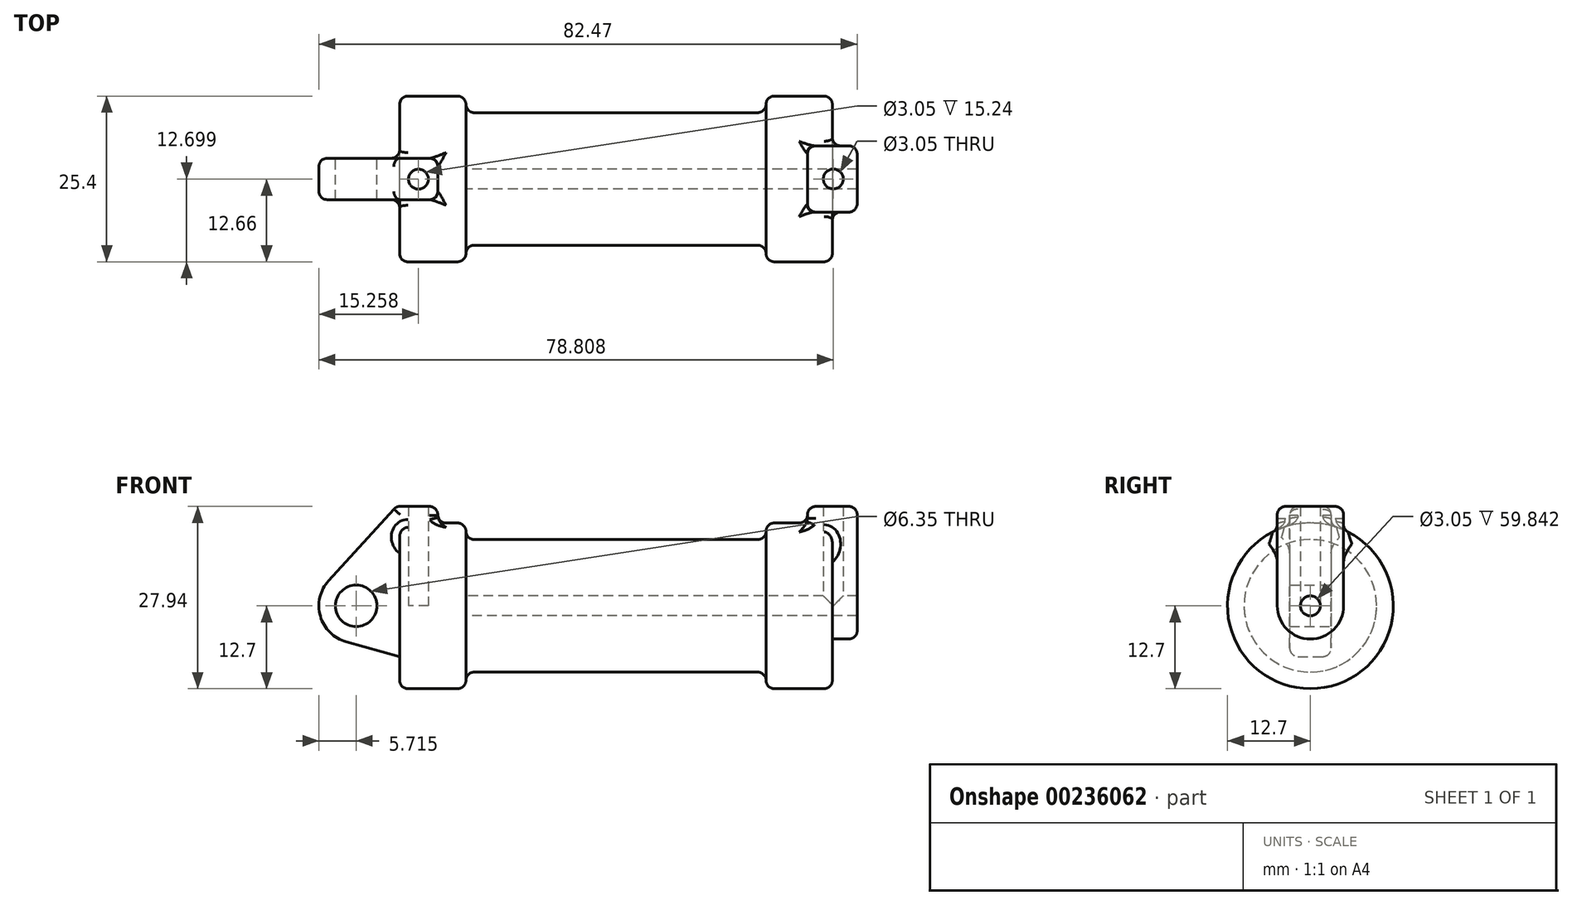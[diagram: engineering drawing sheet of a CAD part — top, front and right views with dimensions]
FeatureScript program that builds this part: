
annotation { "Feature Type Name" : "Feature", "Feature Type Description" : "" }
export const myFeature = defineFeature(function(context is Context, id is Id, definition is map)
    precondition{}
    {
        {
            var Q0;
            Q0=qCreatedBy(makeId("Front.planeOp"),FACE);
            var sketch = newSketch(context, id + "F0", { "sketchPlane" : qUnion([Q0])});
            skLineSegment(sketch, "E0", {"start": v(0, 0) * mm, "end": v(0, 12.7) * mm});
            skLineSegment(sketch, "E1", {"start": v(0, 12.7) * mm, "end": v(10.16, 12.7) * mm});
            skLineSegment(sketch, "E2", {"start": v(10.16, 12.7) * mm, "end": v(10.16, 10.16) * mm});
            skLineSegment(sketch, "E3", {"start": v(10.16, 10.16) * mm, "end": v(56.13, 10.16) * mm});
            skLineSegment(sketch, "E4", {"start": v(56.13, 10.16) * mm, "end": v(56.13, 12.7) * mm});
            skLineSegment(sketch, "E5", {"start": v(56.13, 12.7) * mm, "end": v(66.3, 12.7) * mm});
            skLineSegment(sketch, "E6", {"start": v(66.3, 12.7) * mm, "end": v(66.3, 0) * mm});
            skLineSegment(sketch, "E7", {"start": v(66.3, 0) * mm, "end": v(0, 0) * mm});
            skLineSegment(sketch, "E8", {"start": v(5.84, 15.24) * mm, "end": v(-0.5, 15.24) * mm});
            skLineSegment(sketch, "E9", {"start": v(-0.5, 15.24) * mm, "end": v(-10.88, 3.85) * mm});
            skLineSegment(sketch, "E10", {"start": v(0, 0) * mm, "end": v(-6.65, 0) * mm});
            skCircle(sketch, "E11", {"center": v(-6.65, 0) * mm, "radius": 5.72 * mm});
            skCircle(sketch, "E12", {"center": v(-6.65, 0) * mm, "radius": 3.18 * mm});
            skLineSegment(sketch, "E13", {"start": v(5.84, 15.24) * mm, "end": v(5.84, -9.4) * mm});
            skLineSegment(sketch, "E14", {"start": v(5.84, -9.4) * mm, "end": v(-8.18, -5.5) * mm});
            skSolve(sketch);
        }
        {
            var Q0;
            {var subQ0=sQuery(id+"F0.wireOp",EDGE,"E2");Q0=makeQuery(id+"F0.imprint","IMPRINT",FACE,{"disambiguationData":[TD([[makeQuery(id+"F0.imprint","IMPRINT",EDGE,{"derivedFrom":subQ0}),-1.0]])]});}
            var Q1;
            {var subQ0=sQuery(id+"F0.wireOp",EDGE,"E0");Q1=makeQuery(id+"F0.imprint","IMPRINT",FACE,{"disambiguationData":[TD([[makeQuery(id+"F0.imprint","IMPRINT",EDGE,{"derivedFrom":subQ0}),-1.0]])]});}
            var Q2;
            Q2=sQuery(id+"F0.wireOp",EDGE,"E7");
            revolve(context, id + "F1", {"entities" : qUnion([Q0, Q1]), "axis" : qUnion([Q2]), "revolveType" : RevolveType.FULL});
        }
        {
            var Q0;
            {var subQ0=sQuery(id+"F0.wireOp",EDGE,"E14");Q0=makeQuery(id+"F0.imprint","IMPRINT",FACE,{"disambiguationData":[TD([[makeQuery(id+"F0.imprint","IMPRINT",EDGE,{"derivedFrom":subQ0}),-1.0]])]});}
            var Q1;
            {var subQ4=sQuery(id+"F0.wireOp",EDGE,"E12");Q1=makeQuery(id+"F0.imprint","IMPRINT",FACE,{"disambiguationData":[TD([[makeQuery(id+"F0.imprint","IMPRINT",EDGE,{"derivedFrom":subQ4}),-1.0]])]});}
            var Q2;
            {var subQ3=sQuery(id+"F0.wireOp",EDGE,"E0");Q2=makeQuery(id+"F0.imprint","IMPRINT",FACE,{"disambiguationData":[TD([[makeQuery(id+"F0.imprint","IMPRINT",EDGE,{"derivedFrom":subQ3}),1.0]])]});}
            var Q3;
            {var subQ0=sQuery(id+"F0.wireOp",EDGE,"E0");Q3=makeQuery(id+"F0.imprint","IMPRINT",FACE,{"disambiguationData":[TD([[makeQuery(id+"F0.imprint","IMPRINT",EDGE,{"derivedFrom":subQ0}),-1.0]])]});}
            extrude(context, id + "F2", {"entities" : qUnion([Q0, Q1, Q2, Q3]), "operationType" : NewBodyOperationType.ADD, "endBound" : BoundingType.SYMMETRIC, "depth" : 6.35 * mm});
        }
        {
            var Q0;
            Q0=makeQuery(id+"F1.opRevolve","SWEPT_FACE",FACE,{"disambiguationData":[OSD([sQuery(id+"F0.wireOp",EDGE,"E6")])]});
            var sketch = newSketch(context, id + "F3", { "sketchPlane" : qUnion([Q0])});
            skCircle(sketch, "E15", {"center": v(0, 0) * mm, "radius": 5.08 * mm});
            skCircle(sketch, "E16", {"center": v(0, 0) * mm, "radius": 1.52 * mm});
            skLineSegment(sketch, "E17", {"start": v(5.08, 0) * mm, "end": v(5.08, 15.24) * mm});
            skLineSegment(sketch, "E18", {"start": v(-5.08, 0) * mm, "end": v(-5.08, 15.24) * mm});
            skLineSegment(sketch, "E19", {"start": v(-5.08, 15.24) * mm, "end": v(5.08, 15.24) * mm});
            skSolve(sketch);
        }
        {
            var Q0;
            Q0 = qSketchRegion(id + "F3", true);
            extrude(context, id + "F4", {"entities" : qUnion([Q0]), "operationType" : NewBodyOperationType.ADD, "endBound" : BoundingType.SYMMETRIC, "depth" : 7.62 * mm});
        }
        {
            var Q0;
            Q0=makeQuery(id+"F4.boolean.opBoolean","SPLIT",FACE,{"disambiguationData":[TD([makeQuery(id+"F4.opExtrude","SWEPT_FACE",FACE,{"disambiguationData":[OSD([sQuery(id+"F3.wireOp",EDGE,"E16")])]})])],"derivedFrom":makeQuery(id+"F1.opRevolve","SWEPT_FACE",FACE,{"disambiguationData":[OSD([sQuery(id+"F0.wireOp",EDGE,"E6")])]})});
            extrude(context, id + "F5", {"entities" : qUnion([Q0]), "operationType" : NewBodyOperationType.REMOVE, "oppositeDirection" : true, "depth" : 56.03 * mm});
        }
        {
            var Q0;
            Q0=qCreatedBy(makeId("Top.planeOp"),FACE);
            var sketch = newSketch(context, id + "F6", { "sketchPlane" : qUnion([Q0])});
            skCircle(sketch, "E20", {"center": v(2.89, -0.04) * mm, "radius": 1.52 * mm});
            skSolve(sketch);
        }
        {
            var Q0;
            Q0 = qSketchRegion(id + "F6", true);
            extrude(context, id + "F7", {"entities" : qUnion([Q0]), "operationType" : NewBodyOperationType.REMOVE, "depth" : 17.78 * mm});
        }
        {
            var Q0;
            Q0=qCreatedBy(makeId("Top.planeOp"),FACE);
            var sketch = newSketch(context, id + "F8", { "sketchPlane" : qUnion([Q0])});
            skCircle(sketch, "E21", {"center": v(66.44, 0) * mm, "radius": 1.52 * mm});
            skSolve(sketch);
        }
        {
            var Q0;
            Q0 = qSketchRegion(id + "F8", true);
            extrude(context, id + "F9", {"entities" : qUnion([Q0]), "operationType" : NewBodyOperationType.REMOVE, "depth" : 15.75 * mm});
        }
        {
            var Q0;
            Q0=makeQuery(id+"F1.opRevolve","SWEPT_FACE",FACE,{"disambiguationData":[OSD([sQuery(id+"F0.wireOp",EDGE,"E3")])]});
            var Q1;
            Q1=makeQuery(id+"F1.opRevolve","SWEPT_FACE",FACE,{"disambiguationData":[OSD([sQuery(id+"F0.wireOp",EDGE,"E5")])]});
            var Q2;
            Q2=makeQuery(id+"F1.opRevolve","SWEPT_FACE",FACE,{"disambiguationData":[OSD([sQuery(id+"F0.wireOp",EDGE,"E1")])]});
            fillet(context, id + "F10", {"entities" : qUnion([Q0, Q1, Q2]), "radius" : 1.27 * mm, "tangentPropagation" : true, "allowEdgeOverflow" : false});
        }
        {
            var Q0;
            Q0=makeQuery(id+"F2.opExtrude","CAP_EDGE",EDGE,{"disambiguationData":[OSD([sQuery(id+"F0.wireOp",EDGE,"E9")])],"isStart":false});
            var Q1;
            Q1=makeQuery(id+"F2.opExtrude","CAP_EDGE",EDGE,{"disambiguationData":[OSD([sQuery(id+"F0.wireOp",EDGE,"E8")])],"isStart":false});
            var Q2;
            Q2=makeQuery(id+"F2.opExtrude","CAP_EDGE",EDGE,{"disambiguationData":[OSD([sQuery(id+"F0.wireOp",EDGE,"E13")])],"isStart":false});
            var Q3;
            {var subQ0=makeQuery(id+"F2.opExtrude","CAP_FACE",FACE,{"disambiguationData":[OSD([sQuery(id+"F0.wireOp",EDGE,"E8"),sQuery(id+"F0.wireOp",EDGE,"E9"),sQuery(id+"F0.wireOp",EDGE,"E11"),sQuery(id+"F0.wireOp",EDGE,"E12"),sQuery(id+"F0.wireOp",EDGE,"E13"),sQuery(id+"F0.wireOp",EDGE,"E14")])],"isStart":false});Q3=makeQuery(id+"F10.opFillet","BLEND_EDGE",EDGE,{"blendedFrom":[makeQuery(id+"F2.boolean.opBoolean","INTERSECT",EDGE,{"derivedFrom":[makeQuery(id+"F1.opRevolve","SWEPT_FACE",FACE,{"disambiguationData":[OSD([sQuery(id+"F0.wireOp",EDGE,"E1")])]}),subQ0]}),subQ0],"blendedInto":[subQ0]});}
            var Q4;
            {var subQ0=makeQuery(id+"F2.opExtrude","CAP_FACE",FACE,{"disambiguationData":[OSD([sQuery(id+"F0.wireOp",EDGE,"E8"),sQuery(id+"F0.wireOp",EDGE,"E9"),sQuery(id+"F0.wireOp",EDGE,"E11"),sQuery(id+"F0.wireOp",EDGE,"E12"),sQuery(id+"F0.wireOp",EDGE,"E13"),sQuery(id+"F0.wireOp",EDGE,"E14")])],"isStart":false});Q4=makeQuery(id+"F10.opFillet","BLEND_EDGE",EDGE,{"blendedFrom":[makeQuery(id+"F2.boolean.opBoolean","INTERSECT",VERTEX,{"derivedFrom":[makeQuery(id+"F1.opRevolve","SWEPT_FACE",FACE,{"disambiguationData":[OSD([sQuery(id+"F0.wireOp",EDGE,"E0")])]}),makeQuery(id+"F1.opRevolve","SWEPT_FACE",FACE,{"disambiguationData":[OSD([sQuery(id+"F0.wireOp",EDGE,"E1")])]}),subQ0]}),subQ0],"blendedInto":[subQ0]});}
            var Q5;
            {var subQ0=makeQuery(id+"F2.opExtrude","CAP_FACE",FACE,{"disambiguationData":[OSD([sQuery(id+"F0.wireOp",EDGE,"E8"),sQuery(id+"F0.wireOp",EDGE,"E9"),sQuery(id+"F0.wireOp",EDGE,"E11"),sQuery(id+"F0.wireOp",EDGE,"E12"),sQuery(id+"F0.wireOp",EDGE,"E13"),sQuery(id+"F0.wireOp",EDGE,"E14")])],"isStart":false});Q5=makeQuery(id+"F10.opFillet","BLEND_EDGE",EDGE,{"blendedFrom":[makeQuery(id+"F2.boolean.opBoolean","INTERSECT",EDGE,{"derivedFrom":[makeQuery(id+"F1.opRevolve","SWEPT_FACE",FACE,{"disambiguationData":[OSD([sQuery(id+"F0.wireOp",EDGE,"E0")])]}),subQ0]}),subQ0],"blendedInto":[subQ0]});}
            var Q6;
            Q6=makeQuery(id+"F2.opExtrude","CAP_EDGE",EDGE,{"disambiguationData":[OSD([sQuery(id+"F0.wireOp",EDGE,"E14")])],"isStart":false});
            var Q7;
            Q7=makeQuery(id+"F2.opExtrude","CAP_EDGE",EDGE,{"disambiguationData":[OSD([sQuery(id+"F0.wireOp",EDGE,"E11")])],"isStart":false});
            fillet(context, id + "F11", {"entities" : qUnion([Q0, Q1, Q2, Q3, Q4, Q5, Q6, Q7]), "radius" : 1.27 * mm, "tangentPropagation" : true, "allowEdgeOverflow" : false});
        }
        {
            var Q0;
            Q0=makeQuery(id+"F2.opExtrude","SWEPT_EDGE",EDGE,{"disambiguationData":[OSD([sQuery(id+"F0.wireOp",EDGE,"E8"),sQuery(id+"F0.wireOp",EDGE,"E9")])]});
            var Q1;
            Q1=makeQuery(id+"F2.opExtrude","CAP_EDGE",EDGE,{"disambiguationData":[OSD([sQuery(id+"F0.wireOp",EDGE,"E9")])],"isStart":true});
            var Q2;
            Q2=makeQuery(id+"F2.opExtrude","CAP_EDGE",EDGE,{"disambiguationData":[OSD([sQuery(id+"F0.wireOp",EDGE,"E11")])],"isStart":true});
            var Q3;
            Q3=makeQuery(id+"F2.opExtrude","CAP_EDGE",EDGE,{"disambiguationData":[OSD([sQuery(id+"F0.wireOp",EDGE,"E14")])],"isStart":true});
            fillet(context, id + "F12", {"entities" : qUnion([Q0, Q1, Q2, Q3]), "radius" : 1.27 * mm, "tangentPropagation" : true, "allowEdgeOverflow" : false});
        }
        {
            var Q0;
            Q0=makeQuery(id+"F2.opExtrude","CAP_EDGE",EDGE,{"disambiguationData":[OSD([sQuery(id+"F0.wireOp",EDGE,"E8")])],"isStart":true});
            var Q1;
            Q1=makeQuery(id+"F2.opExtrude","SWEPT_EDGE",EDGE,{"disambiguationData":[OSD([sQuery(id+"F0.wireOp",EDGE,"E8"),sQuery(id+"F0.wireOp",EDGE,"E13")])]});
            fillet(context, id + "F13", {"entities" : qUnion([Q0, Q1]), "radius" : 1.27 * mm, "tangentPropagation" : true, "allowEdgeOverflow" : false});
        }
        {
            var Q0;
            {var subQ0=sQuery(id+"F0.wireOp",EDGE,"E8");Q0=makeQuery(id+"F13.opFillet","BLEND_EDGE",EDGE,{"blendedFrom":[makeQuery(id+"F2.opExtrude","SWEPT_EDGE",EDGE,{"disambiguationData":[OSD([subQ0,sQuery(id+"F0.wireOp",EDGE,"E13")])]}),makeQuery(id+"F2.opExtrude","CAP_EDGE",EDGE,{"disambiguationData":[OSD([subQ0])],"isStart":true})],"blendedInto":[]});}
            fillet(context, id + "F14", {"entities" : qUnion([Q0]), "radius" : 1.27 * mm, "tangentPropagation" : true, "allowEdgeOverflow" : false});
        }
        {
            var Q0;
            Q0=makeQuery(id+"F4.opExtrude","SWEPT_EDGE",EDGE,{"disambiguationData":[OSD([sQuery(id+"F3.wireOp",EDGE,"E18"),sQuery(id+"F3.wireOp",EDGE,"E19")])]});
            var Q1;
            Q1=makeQuery(id+"F4.opExtrude","CAP_EDGE",EDGE,{"disambiguationData":[OSD([sQuery(id+"F3.wireOp",EDGE,"E19")])],"isStart":true});
            var Q2;
            Q2=makeQuery(id+"F4.opExtrude","SWEPT_EDGE",EDGE,{"disambiguationData":[OSD([sQuery(id+"F3.wireOp",EDGE,"E17"),sQuery(id+"F3.wireOp",EDGE,"E19")])]});
            var Q3;
            Q3=makeQuery(id+"F4.opExtrude","CAP_EDGE",EDGE,{"disambiguationData":[OSD([sQuery(id+"F3.wireOp",EDGE,"E19")])],"isStart":false});
            var Q4;
            Q4=makeQuery(id+"F4.opExtrude","CAP_EDGE",EDGE,{"disambiguationData":[OSD([sQuery(id+"F3.wireOp",EDGE,"E17")])],"isStart":false});
            var Q5;
            Q5=makeQuery(id+"F4.opExtrude","CAP_EDGE",EDGE,{"disambiguationData":[OSD([sQuery(id+"F3.wireOp",EDGE,"E15")])],"isStart":false});
            var Q6;
            Q6=makeQuery(id+"F4.opExtrude","CAP_EDGE",EDGE,{"disambiguationData":[OSD([sQuery(id+"F3.wireOp",EDGE,"E18")])],"isStart":false});
            var Q7;
            Q7=makeQuery(id+"F4.opExtrude","CAP_EDGE",EDGE,{"disambiguationData":[OSD([sQuery(id+"F3.wireOp",EDGE,"E18")])],"isStart":true});
            fillet(context, id + "F15", {"entities" : qUnion([Q0, Q1, Q2, Q3, Q4, Q5, Q6, Q7]), "radius" : 1.27 * mm, "tangentPropagation" : true, "allowEdgeOverflow" : false});
        }
        {
            var Q0;
            {var subQ0=sQuery(id+"F3.wireOp",EDGE,"E19");Q0=makeQuery(id+"F15.opFillet","BLEND_EDGE",EDGE,{"blendedFrom":[makeQuery(id+"F4.opExtrude","SWEPT_EDGE",EDGE,{"disambiguationData":[OSD([sQuery(id+"F3.wireOp",EDGE,"E17"),subQ0])]}),makeQuery(id+"F4.opExtrude","CAP_EDGE",EDGE,{"disambiguationData":[OSD([subQ0])],"isStart":true})],"blendedInto":[]});}
            fillet(context, id + "F16", {"entities" : qUnion([Q0]), "radius" : 1.27 * mm, "tangentPropagation" : true, "allowEdgeOverflow" : false});
        }
    });
